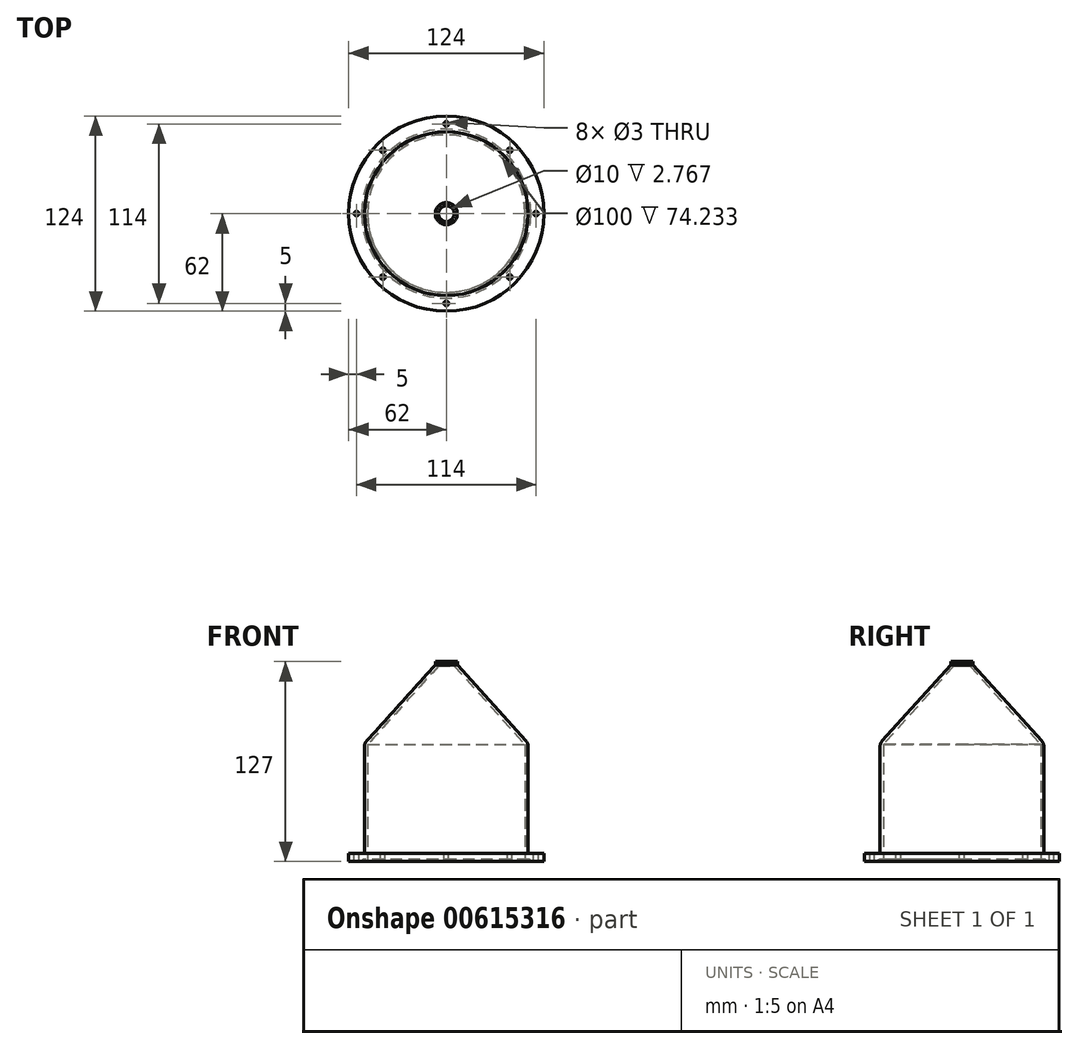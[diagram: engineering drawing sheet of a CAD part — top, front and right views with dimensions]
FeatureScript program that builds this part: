
annotation { "Feature Type Name" : "Feature", "Feature Type Description" : "" }
export const myFeature = defineFeature(function(context is Context, id is Id, definition is map)
    precondition{}
    {
        {
            var Q0;
            Q0=qCreatedBy(makeId("Top.planeOp"),FACE);
            var sketch = newSketch(context, id + "F0", { "sketchPlane" : qUnion([Q0])});
            skCircle(sketch, "E0", {"center": v(0, 0) * mm, "radius": 52 * mm});
            skSolve(sketch);
        }
        {
            var Q0;
            Q0 = qSketchRegion(id + "F0", true);
            extrude(context, id + "F1", {"entities" : qUnion([Q0]), "depth" : 75 * mm, "offsetDistance" : 25 * mm});
        }
        {
            var Q0;
            Q0=makeQuery(id+"F1.opExtrude","CAP_FACE",FACE,{"disambiguationData":[OSD([sQuery(id+"F0.wireOp",EDGE,"E0")])],"isStart":false});
            var sketch = newSketch(context, id + "F2", { "sketchPlane" : qUnion([Q0])});
            skCircle(sketch, "E1", {"center": v(0, 0) * mm, "radius": 7 * mm});
            skSolve(sketch);
        }
        {
            var Q0;
            Q0 = qSketchRegion(id + "F2", true);
            extrude(context, id + "F3", {"entities" : qUnion([Q0]), "depth" : 2 * mm, "offsetDistance" : 25 * mm});
        }
        {
            var Q0;
            Q0=makeQuery(id+"F3.opExtrude","SWEPT_BODY",BODY,{"disambiguationData":[OSD([sQuery(id+"F2.wireOp",EDGE,"E1")])]});
            transform(context, id + "F4", {"entities" : qUnion([Q0]), "transformType" : TransformType.TRANSLATION_3D, "dx" : 0 * mm, "dy" : 0 * mm, "dz" : 50 * mm, "makeCopy" : false});
        }
        {
            var Q0;
            Q0=makeQuery(id+"F1.opExtrude","CAP_FACE",FACE,{"disambiguationData":[OSD([sQuery(id+"F0.wireOp",EDGE,"E0")])],"isStart":false});
            var Q1;
            Q1=makeQuery(id+"F3.opExtrude","CAP_FACE",FACE,{"disambiguationData":[OSD([sQuery(id+"F2.wireOp",EDGE,"E1")])],"isStart":true});
            loft(context, id + "F5", {"sheetProfilesArray" : [{ "sheetProfileEntities" : qUnion([Q0]) }, { "sheetProfileEntities" : qUnion([Q1]) }]});
        }
        {
            var Q0;
            Q0=makeQuery(id+"F5.opLoft","SWEPT_BODY",BODY,{"disambiguationData":[OSD([sQuery(id+"F0.wireOp",EDGE,"E0"),sQuery(id+"F2.wireOp",EDGE,"E1")])]});
            var Q1;
            Q1=makeQuery(id+"F3.opExtrude","SWEPT_BODY",BODY,{"disambiguationData":[OSD([sQuery(id+"F2.wireOp",EDGE,"E1")])]});
            var Q2;
            Q2=makeQuery(id+"F1.opExtrude","SWEPT_BODY",BODY,{"disambiguationData":[OSD([sQuery(id+"F0.wireOp",EDGE,"E0")])]});
            booleanBodies(context, id + "F6", {"operationType" : BooleanOperationType.UNION, "tools" : qUnion([Q0, Q1, Q2])});
        }
        {
            var Q0;
            Q0=makeQuery(id+"F1.opExtrude","CAP_FACE",FACE,{"disambiguationData":[OSD([sQuery(id+"F0.wireOp",EDGE,"E0")])],"isStart":true});
            shell(context, id + "F7", {"entities" : qUnion([Q0]), "thickness" : 2 * mm});
        }
        {
            var Q0;
            Q0=makeQuery(id+"F3.opExtrude","CAP_FACE",FACE,{"disambiguationData":[OSD([sQuery(id+"F2.wireOp",EDGE,"E1")])],"isStart":false});
            var sketch = newSketch(context, id + "F8", { "sketchPlane" : qUnion([Q0])});
            skCircle(sketch, "E2", {"center": v(0, 0) * mm, "radius": 5 * mm});
            skSolve(sketch);
        }
        {
            var Q0;
            Q0=makeQuery(id+"F8.imprint","IMPRINT",FACE,{"disambiguationData":[TD([[makeQuery(id+"F8.imprint","IMPRINT",EDGE,{"derivedFrom":sQuery(id+"F8.wireOp",EDGE,"E2")}),1.0]])]});
            extrude(context, id + "F9", {"entities" : qUnion([Q0]), "operationType" : NewBodyOperationType.REMOVE, "oppositeDirection" : true, "depth" : 25 * mm, "offsetDistance" : 25 * mm});
        }
        {
            var Q0;
            Q0=makeQuery(id+"F1.opExtrude","CAP_FACE",FACE,{"disambiguationData":[OSD([sQuery(id+"F0.wireOp",EDGE,"E0")])],"isStart":true});
            var sketch = newSketch(context, id + "F10", { "sketchPlane" : qUnion([Q0])});
            skCircle(sketch, "E3", {"center": v(0, 0) * mm, "radius": 62 * mm});
            skSolve(sketch);
        }
        {
            var Q0;
            Q0=makeQuery(id+"F10.imprint","IMPRINT",FACE,{"disambiguationData":[TD([[makeQuery(id+"F10.imprint","IMPRINT",EDGE,{"derivedFrom":sQuery(id+"F10.wireOp",EDGE,"E3")}),1.0]])]});
            extrude(context, id + "F11", {"entities" : qUnion([Q0]), "operationType" : NewBodyOperationType.ADD, "oppositeDirection" : true, "depth" : 5 * mm, "offsetDistance" : 25 * mm});
        }
        {
            var Q0;
            Q0=makeQuery(id+"F11.opExtrude","CAP_FACE",FACE,{"disambiguationData":[OSD([sQuery(id+"F0.wireOp",EDGE,"E0"),sQuery(id+"F10.wireOp",EDGE,"E3")])],"isStart":false});
            var sketch = newSketch(context, id + "F12", { "sketchPlane" : qUnion([Q0])});
            skLineSegment(sketch, "E4", {"start": v(0, 62) * mm, "end": v(0, 52) * mm});
            skPoint(sketch, "E5", {"position": v(0, 57) * mm});
            skPoint(sketch, "E6.1.0", {"position": v(-40.3, 40.3) * mm});
            skPoint(sketch, "E6.2.0", {"position": v(-57, 0) * mm});
            skPoint(sketch, "E6.3.0", {"position": v(-40.3, -40.3) * mm});
            skPoint(sketch, "E6.4.0", {"position": v(0, -57) * mm});
            skPoint(sketch, "E6.5.0", {"position": v(40.3, -40.3) * mm});
            skPoint(sketch, "E6.6.0", {"position": v(57, 0) * mm});
            skPoint(sketch, "E6.7.0", {"position": v(40.3, 40.3) * mm});
            skPoint(sketch, "E6.center", {"position": v(0, 0) * mm});
            skSolve(sketch);
        }
        {
            var Q0;
            Q0=sQuery(id+"F12.wireOp",VERTEX,"E5");
            var Q1;
            Q1=sQuery(id+"F12.wireOp",VERTEX,"E6.7.0");
            var Q2;
            Q2=sQuery(id+"F12.wireOp",VERTEX,"E6.6.0");
            var Q3;
            Q3=sQuery(id+"F12.wireOp",VERTEX,"E6.5.0");
            var Q4;
            Q4=sQuery(id+"F12.wireOp",VERTEX,"E6.4.0");
            var Q5;
            Q5=sQuery(id+"F12.wireOp",VERTEX,"E6.3.0");
            var Q6;
            Q6=sQuery(id+"F12.wireOp",VERTEX,"E6.2.0");
            var Q7;
            Q7=sQuery(id+"F12.wireOp",VERTEX,"E6.1.0");
            var Q8;
            Q8=makeQuery(id+"F5.opLoft","SWEPT_BODY",BODY,{"disambiguationData":[OSD([sQuery(id+"F0.wireOp",EDGE,"E0"),sQuery(id+"F2.wireOp",EDGE,"E1")])]});
            hole(context, id + "F13", {"style" : HoleStyle.SIMPLE, "endStyle" : HoleEndStyle.THROUGH, "holeDiameter" : 3 * mm, "majorDiameter" : 5 * mm, "isTappedThrough" : true, "tappedDepth" : 12 * mm, "tapClearance" : 3, "locations" : qUnion([Q0, Q1, Q2, Q3, Q4, Q5, Q6, Q7]), "scope" : qUnion([Q8])});
        }
        {
            var Q0;
            {var subQ0=sQuery(id+"F0.wireOp",EDGE,"E0");Q0=makeQuery(id+"F11.boolean.opBoolean","MERGE",FACE,{"derivedFrom":[makeQuery(id+"F1.opExtrude","CAP_FACE",FACE,{"disambiguationData":[OSD([subQ0])],"isStart":true}),makeQuery(id+"F11.opExtrude","CAP_FACE",FACE,{"disambiguationData":[OSD([subQ0,sQuery(id+"F10.wireOp",EDGE,"E3")])],"isStart":true})]});}
            var sketch = newSketch(context, id + "F14", { "sketchPlane" : qUnion([Q0])});
            skCircle(sketch, "E7", {"center": v(0, 0) * mm, "radius": 52.5 * mm});
            skSolve(sketch);
        }
        {
            var Q0;
            Q0=qCreatedBy(makeId("Front.planeOp"),FACE);
            var sketch = newSketch(context, id + "F15", { "sketchPlane" : qUnion([Q0])});
            skCircle(sketch, "E8", {"center": v(-52.48, 0) * mm, "radius": 1.25 * mm});
            skSolve(sketch);
        }
        {
            var Q0;
            Q0=makeQuery(id+"F15.imprint","IMPRINT",FACE,{"disambiguationData":[TD([[makeQuery(id+"F15.imprint","IMPRINT",EDGE,{"derivedFrom":sQuery(id+"F15.wireOp",EDGE,"E8")}),1.0]])]});
            var Q1;
            Q1=sQuery(id+"F14.wireOp",EDGE,"E7");
            sweep(context, id + "F16", {"operationType" : NewBodyOperationType.REMOVE, "profiles" : qUnion([Q0]), "path" : qUnion([Q1])});
        }
        {
            var Q0;
            {var subQ0=sQuery(id+"F0.wireOp",EDGE,"E0");Q0=makeQuery(id+"F6.opBoolean","MERGE",EDGE,{"derivedFrom":[makeQuery(id+"F1.opExtrude","CAP_EDGE",EDGE,{"disambiguationData":[OSD([subQ0])],"isStart":false}),makeQuery(id+"F5.opLoft","MID_CAP_EDGE",EDGE,{"disambiguationData":[OSD([subQ0])],"capPos":0.0})]});}
            fillet(context, id + "F17", {"entities" : qUnion([Q0]), "radius" : 5 * mm, "tangentPropagation" : true, "allowEdgeOverflow" : false});
        }
    });
